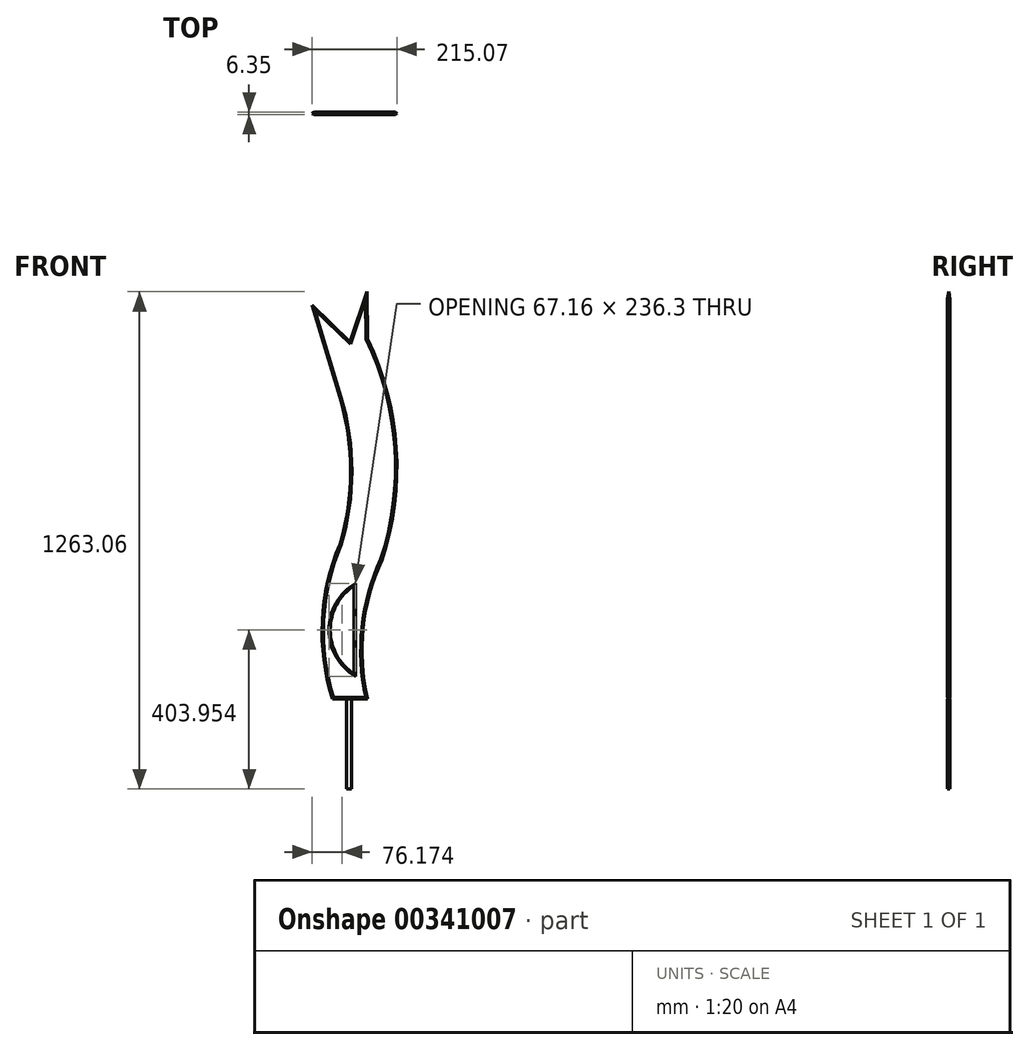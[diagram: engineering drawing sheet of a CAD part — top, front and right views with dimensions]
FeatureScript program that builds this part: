
annotation { "Feature Type Name" : "Feature", "Feature Type Description" : "" }
export const myFeature = defineFeature(function(context is Context, id is Id, definition is map)
    precondition{}
    {
        {
            var Q0;
            Q0=qCreatedBy(makeId("Front.planeOp"),FACE);
            var sketch = newSketch(context, id + "F0", { "sketchPlane" : qUnion([Q0])});
            skLineSegment(sketch, "E0", {"start": v(-19.15, -12.58) * mm, "end": v(69.75, -12.58) * mm});
            skArc(sketch, "E1", {"start": v(0, 379.7) * mm, "mid": v(-44.75, 185.28) * mm, "end": v(-19.15, -12.58) * mm});
            skArc(sketch, "E2", {"start": v(0, 379.7) * mm, "mid": v(27.32, 566.09) * mm, "end": v(0, 752.48) * mm});
            skLineSegment(sketch, "E3", {"start": v(0, 752.48) * mm, "end": v(-70.48, 987.7) * mm});
            skLineSegment(sketch, "E4", {"start": v(-70.48, 987.7) * mm, "end": v(25.45, 894.5) * mm});
            skLineSegment(sketch, "E5", {"start": v(25.45, 894.5) * mm, "end": v(68.38, 1021.76) * mm});
            skLineSegment(sketch, "E6", {"start": v(68.38, 1021.76) * mm, "end": v(69.75, 901.82) * mm});
            skArc(sketch, "E7", {"start": v(106.5, 340.2) * mm, "mid": v(143, 624.6) * mm, "end": v(69.75, 901.82) * mm});
            skArc(sketch, "E8", {"start": v(106.5, 340.2) * mm, "mid": v(58.94, 166.86) * mm, "end": v(69.75, -12.58) * mm});
            skSolve(sketch);
        }
        {
            var Q0;
            Q0=makeQuery(id+"F0.imprint","IMPRINT",FACE,{"disambiguationData":[TD([[makeQuery(id+"F0.imprint","IMPRINT",EDGE,{"derivedFrom":sQuery(id+"F0.wireOp",EDGE,"E0")}),1.0]])]});
            extrude(context, id + "F1", {"entities" : qUnion([Q0]), "depth" : 6.35 * mm});
        }
        {
            var Q0;
            Q0=makeQuery(id+"F1.opExtrude","CAP_FACE",FACE,{"disambiguationData":[OSD([sQuery(id+"F0.wireOp",EDGE,"E0"),sQuery(id+"F0.wireOp",EDGE,"cmRgr26G-jsff-BSfF-MUjK-vPcJ23yHo0d1"),sQuery(id+"F0.wireOp",EDGE,"E1"),sQuery(id+"F0.wireOp",EDGE,"E2"),sQuery(id+"F0.wireOp",EDGE,"E3"),sQuery(id+"F0.wireOp",EDGE,"E4"),sQuery(id+"F0.wireOp",EDGE,"E5"),sQuery(id+"F0.wireOp",EDGE,"E6")])],"isStart":false});
            var sketch = newSketch(context, id + "F2", { "sketchPlane" : qUnion([Q0])});
            skLineSegment(sketch, "E9", {"start": v(36.1, 275.08) * mm, "end": v(36.1, 50.23) * mm});
            skArc(sketch, "E10", {"start": v(36.1, 275.08) * mm, "mid": v(-24.71, 162.65) * mm, "end": v(36.1, 50.23) * mm});
            skSolve(sketch);
        }
        {
            var Q0;
            Q0=makeQuery(id+"F2.imprint","IMPRINT",FACE,{"disambiguationData":[TD([[makeQuery(id+"F2.imprint","IMPRINT",EDGE,{"derivedFrom":sQuery(id+"F2.wireOp",EDGE,"E9")}),-1.0]])]});
            extrude(context, id + "F3", {"entities" : qUnion([Q0]), "operationType" : NewBodyOperationType.REMOVE, "oppositeDirection" : true, "depth" : 25.4 * mm});
        }
        {
            var Q0;
            Q0=makeQuery(id+"F1.opExtrude","CAP_EDGE",EDGE,{"disambiguationData":[OSD([sQuery(id+"F0.wireOp",EDGE,"E4")])],"isStart":true});
            var Q1;
            Q1=makeQuery(id+"F1.opExtrude","CAP_EDGE",EDGE,{"disambiguationData":[OSD([sQuery(id+"F0.wireOp",EDGE,"E4")])],"isStart":false});
            var Q2;
            Q2=makeQuery(id+"F1.opExtrude","CAP_EDGE",EDGE,{"disambiguationData":[OSD([sQuery(id+"F0.wireOp",EDGE,"E6")])],"isStart":false});
            var Q3;
            Q3=makeQuery(id+"F1.opExtrude","CAP_EDGE",EDGE,{"disambiguationData":[OSD([sQuery(id+"F0.wireOp",EDGE,"E5")])],"isStart":false});
            var Q4;
            Q4=makeQuery(id+"F1.opExtrude","CAP_EDGE",EDGE,{"disambiguationData":[OSD([sQuery(id+"F0.wireOp",EDGE,"E6")])],"isStart":true});
            var Q5;
            Q5=makeQuery(id+"F1.opExtrude","CAP_EDGE",EDGE,{"disambiguationData":[OSD([sQuery(id+"F0.wireOp",EDGE,"E7")])],"isStart":true});
            var Q6;
            Q6=makeQuery(id+"F1.opExtrude","CAP_EDGE",EDGE,{"disambiguationData":[OSD([sQuery(id+"F0.wireOp",EDGE,"E8")])],"isStart":true});
            var Q7;
            Q7=makeQuery(id+"F1.opExtrude","CAP_EDGE",EDGE,{"disambiguationData":[OSD([sQuery(id+"F0.wireOp",EDGE,"E8")])],"isStart":false});
            var Q8;
            Q8=makeQuery(id+"F1.opExtrude","CAP_EDGE",EDGE,{"disambiguationData":[OSD([sQuery(id+"F0.wireOp",EDGE,"E7")])],"isStart":false});
            var Q9;
            Q9=makeQuery(id+"F1.opExtrude","CAP_EDGE",EDGE,{"disambiguationData":[OSD([sQuery(id+"F0.wireOp",EDGE,"E3")])],"isStart":false});
            var Q10;
            Q10=makeQuery(id+"F1.opExtrude","CAP_EDGE",EDGE,{"disambiguationData":[OSD([sQuery(id+"F0.wireOp",EDGE,"E2")])],"isStart":false});
            var Q11;
            Q11=makeQuery(id+"F1.opExtrude","CAP_FACE",FACE,{"disambiguationData":[OSD([sQuery(id+"F0.wireOp",EDGE,"E0"),sQuery(id+"F0.wireOp",EDGE,"E1"),sQuery(id+"F0.wireOp",EDGE,"E2"),sQuery(id+"F0.wireOp",EDGE,"E3"),sQuery(id+"F0.wireOp",EDGE,"E4"),sQuery(id+"F0.wireOp",EDGE,"E5"),sQuery(id+"F0.wireOp",EDGE,"E6"),sQuery(id+"F0.wireOp",EDGE,"E7"),sQuery(id+"F0.wireOp",EDGE,"E8")])],"isStart":false});
            var Q12;
            Q12=makeQuery(id+"F1.opExtrude","CAP_EDGE",EDGE,{"disambiguationData":[OSD([sQuery(id+"F0.wireOp",EDGE,"E1")])],"isStart":true});
            var Q13;
            Q13=makeQuery(id+"F1.opExtrude","CAP_EDGE",EDGE,{"disambiguationData":[OSD([sQuery(id+"F0.wireOp",EDGE,"E2")])],"isStart":true});
            var Q14;
            Q14=makeQuery(id+"F1.opExtrude","CAP_EDGE",EDGE,{"disambiguationData":[OSD([sQuery(id+"F0.wireOp",EDGE,"E5")])],"isStart":true});
            var Q15;
            Q15=makeQuery(id+"F1.opExtrude","CAP_FACE",FACE,{"disambiguationData":[OSD([sQuery(id+"F0.wireOp",EDGE,"E0"),sQuery(id+"F0.wireOp",EDGE,"E1"),sQuery(id+"F0.wireOp",EDGE,"E2"),sQuery(id+"F0.wireOp",EDGE,"E3"),sQuery(id+"F0.wireOp",EDGE,"E4"),sQuery(id+"F0.wireOp",EDGE,"E5"),sQuery(id+"F0.wireOp",EDGE,"E6"),sQuery(id+"F0.wireOp",EDGE,"E7"),sQuery(id+"F0.wireOp",EDGE,"E8")])],"isStart":true});
            chamfer(context, id + "F4", {"entities" : qUnion([Q0, Q1, Q2, Q3, Q4, Q5, Q6, Q7, Q8, Q9, Q10, Q11, Q12, Q13, Q14, Q15]), "width" : 3.17 * mm, "tangentPropagation" : true});
        }
        {
            var Q0;
            Q0=qCreatedBy(makeId("Top.planeOp"),FACE);
            cPlane(context, id + "F5", {"entities" : qUnion([Q0]), "cplaneType" : CPlaneType.OFFSET, "offset" : 12.7 * mm, "oppositeDirection" : true, "width" : 152.4 * mm, "height" : 152.4 * mm});
        }
        {
            var Q0;
            Q0=qCreatedBy(id+"F5.planeOp",FACE);
            var sketch = newSketch(context, id + "F6", { "sketchPlane" : qUnion([Q0])});
            skLineSegment(sketch, "E11.bottom", {"start": v(17.26, 0) * mm, "end": v(29.96, 0) * mm});
            skLineSegment(sketch, "E11.top", {"start": v(17.26, -6.35) * mm, "end": v(29.96, -6.35) * mm});
            skLineSegment(sketch, "E11.left", {"start": v(17.26, 0) * mm, "end": v(17.26, -6.35) * mm});
            skLineSegment(sketch, "E11.right", {"start": v(29.96, 0) * mm, "end": v(29.96, -6.35) * mm});
            skSolve(sketch);
        }
        {
            var Q0;
            Q0=makeQuery(id+"F6.imprint","IMPRINT",FACE,{"disambiguationData":[TD([[makeQuery(id+"F6.imprint","IMPRINT",EDGE,{"derivedFrom":sQuery(id+"F6.wireOp",EDGE,"E11.bottom")}),-1.0]])]});
            extrude(context, id + "F7", {"entities" : qUnion([Q0]), "operationType" : NewBodyOperationType.ADD, "oppositeDirection" : true, "depth" : 228.6 * mm});
        }
    });
